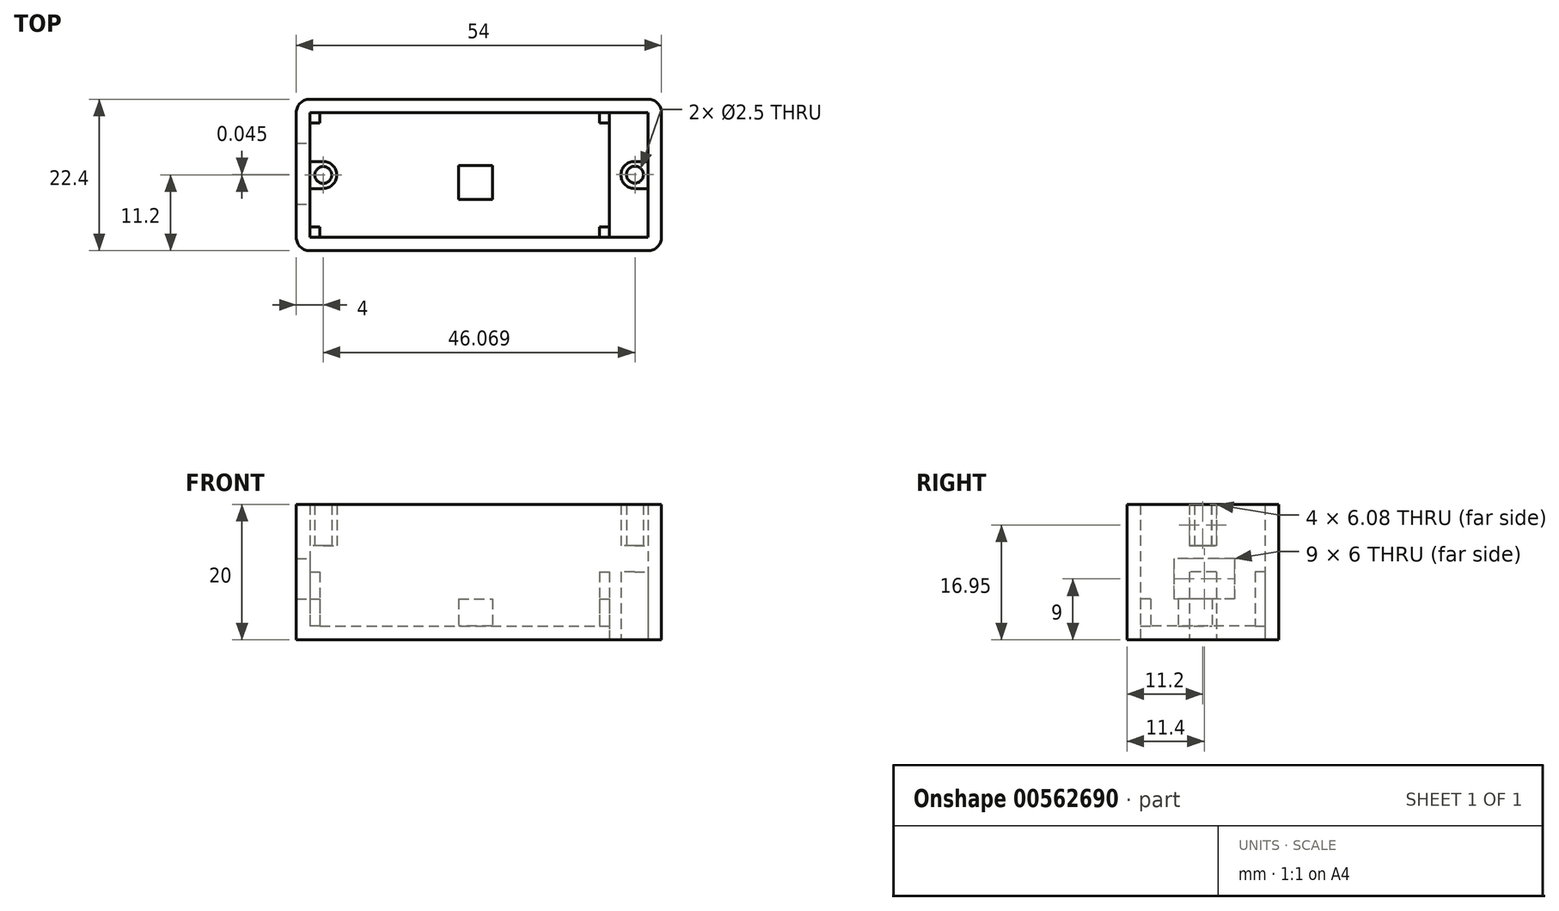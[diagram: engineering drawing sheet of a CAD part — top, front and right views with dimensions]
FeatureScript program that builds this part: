
annotation { "Feature Type Name" : "Feature", "Feature Type Description" : "" }
export const myFeature = defineFeature(function(context is Context, id is Id, definition is map)
    precondition{}
    {
        {
            var Q0;
            Q0=qCreatedBy(makeId("Top.planeOp"),FACE);
            var sketch = newSketch(context, id + "F0", { "sketchPlane" : qUnion([Q0])});
            skLineSegment(sketch, "E0.bottom", {"start": v(-31.58, 11.2) * mm, "end": v(22.42, 11.2) * mm});
            skLineSegment(sketch, "E0.top", {"start": v(-31.58, -11.2) * mm, "end": v(22.42, -11.2) * mm});
            skLineSegment(sketch, "E0.left", {"start": v(-31.58, 11.2) * mm, "end": v(-31.58, -11.2) * mm});
            skLineSegment(sketch, "E0.right", {"start": v(22.42, 11.2) * mm, "end": v(22.42, -11.2) * mm});
            skLineSegment(sketch, "E1.bottom", {"start": v(-29.58, 9.2) * mm, "end": v(20.42, 9.2) * mm});
            skLineSegment(sketch, "E1.top", {"start": v(-29.58, -9.2) * mm, "end": v(20.42, -9.2) * mm});
            skLineSegment(sketch, "E1.left", {"start": v(-29.58, 9.2) * mm, "end": v(-29.58, -9.2) * mm});
            skLineSegment(sketch, "E1.right", {"start": v(20.42, 9.2) * mm, "end": v(20.42, -9.2) * mm});
            skCircle(sketch, "E2", {"center": v(18.42, 0) * mm, "radius": 2 * mm});
            skCircle(sketch, "E3", {"center": v(-27.58, 0) * mm, "radius": 2 * mm});
            skLineSegment(sketch, "E4.bottom", {"start": v(-27.58, -2) * mm, "end": v(-29.58, -2) * mm});
            skLineSegment(sketch, "E4.top", {"start": v(-27.58, 2) * mm, "end": v(-29.58, 2) * mm});
            skLineSegment(sketch, "E4.left", {"start": v(-27.58, -2) * mm, "end": v(-27.58, 2) * mm});
            skLineSegment(sketch, "E4.right", {"start": v(-29.58, -2) * mm, "end": v(-29.58, 2) * mm});
            skLineSegment(sketch, "E5.bottom", {"start": v(18.42, 2) * mm, "end": v(20.42, 2) * mm});
            skLineSegment(sketch, "E5.top", {"start": v(18.42, -2) * mm, "end": v(20.42, -2) * mm});
            skLineSegment(sketch, "E5.left", {"start": v(18.42, 2) * mm, "end": v(18.42, -2) * mm});
            skLineSegment(sketch, "E5.right", {"start": v(20.42, 2) * mm, "end": v(20.42, -2) * mm});
            skCircle(sketch, "E6", {"center": v(-27.58, 0) * mm, "radius": 1.25 * mm});
            skCircle(sketch, "E7", {"center": v(18.49, 0.05) * mm, "radius": 1.25 * mm});
            skLineSegment(sketch, "E8.bottom", {"start": v(-29.58, 9.2) * mm, "end": v(14.72, 9.2) * mm});
            skLineSegment(sketch, "E8.top", {"start": v(-29.58, -9.2) * mm, "end": v(14.72, -9.2) * mm});
            skLineSegment(sketch, "E8.right", {"start": v(14.72, 9.2) * mm, "end": v(14.72, -9.2) * mm});
            skLineSegment(sketch, "E9.bottom", {"start": v(-7.58, 1.37) * mm, "end": v(-2.58, 1.37) * mm});
            skLineSegment(sketch, "E9.top", {"start": v(-7.58, -3.63) * mm, "end": v(-2.58, -3.63) * mm});
            skLineSegment(sketch, "E9.left", {"start": v(-7.58, 1.37) * mm, "end": v(-7.58, -3.63) * mm});
            skLineSegment(sketch, "E9.right", {"start": v(-2.58, 1.37) * mm, "end": v(-2.58, -3.63) * mm});
            skLineSegment(sketch, "E10.bottom", {"start": v(-28.08, 9.2) * mm, "end": v(-29.58, 9.2) * mm});
            skLineSegment(sketch, "E10.top", {"start": v(-28.08, 7.7) * mm, "end": v(-29.58, 7.7) * mm});
            skLineSegment(sketch, "E10.left", {"start": v(-28.08, 9.2) * mm, "end": v(-28.08, 7.7) * mm});
            skLineSegment(sketch, "E10.right", {"start": v(-29.58, 9.2) * mm, "end": v(-29.58, 7.7) * mm});
            skLineSegment(sketch, "E11.bottom", {"start": v(-29.58, -7.7) * mm, "end": v(-28.08, -7.7) * mm});
            skLineSegment(sketch, "E11.top", {"start": v(-29.58, -9.2) * mm, "end": v(-28.08, -9.2) * mm});
            skLineSegment(sketch, "E11.left", {"start": v(-29.58, -7.7) * mm, "end": v(-29.58, -9.2) * mm});
            skLineSegment(sketch, "E11.right", {"start": v(-28.08, -7.7) * mm, "end": v(-28.08, -9.2) * mm});
            skLineSegment(sketch, "E12.bottom", {"start": v(13.22, 9.2) * mm, "end": v(14.72, 9.2) * mm});
            skLineSegment(sketch, "E12.top", {"start": v(13.22, 7.7) * mm, "end": v(14.72, 7.7) * mm});
            skLineSegment(sketch, "E12.left", {"start": v(13.22, 9.2) * mm, "end": v(13.22, 7.7) * mm});
            skLineSegment(sketch, "E12.right", {"start": v(14.72, 9.2) * mm, "end": v(14.72, 7.7) * mm});
            skLineSegment(sketch, "E13.bottom", {"start": v(14.72, -7.7) * mm, "end": v(13.22, -7.7) * mm});
            skLineSegment(sketch, "E13.top", {"start": v(14.72, -9.2) * mm, "end": v(13.22, -9.2) * mm});
            skLineSegment(sketch, "E13.left", {"start": v(14.72, -7.7) * mm, "end": v(14.72, -9.2) * mm});
            skLineSegment(sketch, "E13.right", {"start": v(13.22, -7.7) * mm, "end": v(13.22, -9.2) * mm});
            skSolve(sketch);
        }
        {
            var Q0;
            Q0=qSketchRegion(id+"F0",true);
            extrude(context, id + "F1", {"entities" : qUnion([Q0]), "depth" : 20 * mm});
        }
        {
            var Q0;
            Q0=makeQuery(id+"F0.imprint","IMPRINT",FACE,{"disambiguationData":[TD([[makeQuery(id+"F0.imprint","IMPRINT",EDGE,{"derivedFrom":sQuery(id+"F0.wireOp",EDGE,"E1.bottom")}),-1.0]])]});
            var Q1;
            {var subQ2=sQuery(id+"F0.wireOp",EDGE,"E4.bottom");Q1=makeQuery(id+"F0.imprint","IMPRINT",FACE,{"disambiguationData":[TD([[makeQuery(id+"F0.imprint","IMPRINT",EDGE,{"derivedFrom":subQ2}),1.0]])]});}
            var Q2;
            {var subQ0=sQuery(id+"F0.wireOp",EDGE,"E5.left");var subQ3=sQuery(id+"F0.wireOp",EDGE,"E7");var subQ5=makeQuery(id+"F0.imprint","INTERSECT",VERTEX,{"disambiguationData":[OD(0.0)],"derivedFrom":[subQ0,subQ3]});Q2=makeQuery(id+"F0.imprint","IMPRINT",FACE,{"disambiguationData":[TD([[makeQuery(id+"F0.imprint","IMPRINT",EDGE,{"disambiguationData":[TD([[subQ5,1.0]])],"derivedFrom":subQ3}),-1.0]])]});}
            var Q3;
            {var subQ0=sQuery(id+"F0.wireOp",EDGE,"E5.bottom");Q3=makeQuery(id+"F0.imprint","IMPRINT",FACE,{"disambiguationData":[TD([[makeQuery(id+"F0.imprint","IMPRINT",EDGE,{"derivedFrom":subQ0}),-1.0]])]});}
            var Q4;
            {var subQ0=sQuery(id+"F0.wireOp",EDGE,"E5.top");Q4=makeQuery(id+"F0.imprint","IMPRINT",FACE,{"disambiguationData":[TD([[makeQuery(id+"F0.imprint","IMPRINT",EDGE,{"derivedFrom":subQ0}),1.0]])]});}
            var Q5;
            {var subQ0=sQuery(id+"F0.wireOp",EDGE,"E5.left");var subQ4=sQuery(id+"F0.wireOp",EDGE,"E7");var subQ5=makeQuery(id+"F0.imprint","INTERSECT",VERTEX,{"disambiguationData":[OD(0.0)],"derivedFrom":[subQ0,subQ4]});Q5=makeQuery(id+"F0.imprint","IMPRINT",FACE,{"disambiguationData":[TD([[makeQuery(id+"F0.imprint","IMPRINT",EDGE,{"disambiguationData":[TD([[subQ5,-1.0]])],"derivedFrom":subQ4}),-1.0]])]});}
            var Q6;
            {var subQ0=sQuery(id+"F0.wireOp",EDGE,"E7");var subQ1=sQuery(id+"F0.wireOp",EDGE,"E5.left");var subQ2=makeQuery(id+"F0.imprint","INTERSECT",VERTEX,{"disambiguationData":[OD(0.0)],"derivedFrom":[subQ1,subQ0]});Q6=makeQuery(id+"F0.imprint","IMPRINT",FACE,{"disambiguationData":[TD([[makeQuery(id+"F0.imprint","IMPRINT",EDGE,{"disambiguationData":[TD([[subQ2,-1.0]])],"derivedFrom":subQ1}),-1.0]])]});}
            var Q7;
            {var subQ0=sQuery(id+"F0.wireOp",EDGE,"E7");var subQ1=sQuery(id+"F0.wireOp",EDGE,"E5.left");var subQ2=makeQuery(id+"F0.imprint","INTERSECT",VERTEX,{"disambiguationData":[OD(0.0)],"derivedFrom":[subQ1,subQ0]});Q7=makeQuery(id+"F0.imprint","IMPRINT",FACE,{"disambiguationData":[TD([[makeQuery(id+"F0.imprint","IMPRINT",EDGE,{"disambiguationData":[TD([[subQ2,-1.0]])],"derivedFrom":subQ1}),1.0]])]});}
            var Q8;
            {var subQ0=sQuery(id+"F0.wireOp",EDGE,"E4.top");Q8=makeQuery(id+"F0.imprint","IMPRINT",FACE,{"disambiguationData":[TD([[makeQuery(id+"F0.imprint","IMPRINT",EDGE,{"derivedFrom":subQ0}),1.0]])]});}
            var Q9;
            {var subQ0=sQuery(id+"F0.wireOp",EDGE,"E4.bottom");Q9=makeQuery(id+"F0.imprint","IMPRINT",FACE,{"disambiguationData":[TD([[makeQuery(id+"F0.imprint","IMPRINT",EDGE,{"derivedFrom":subQ0}),-1.0]])]});}
            var Q10;
            {var subQ0=sQuery(id+"F0.wireOp",EDGE,"E4.left");var subQ3=sQuery(id+"F0.wireOp",EDGE,"E6");var subQ6=makeQuery(id+"F0.imprint","INTERSECT",VERTEX,{"disambiguationData":[OD(0.0)],"derivedFrom":[subQ0,subQ3]});Q10=makeQuery(id+"F0.imprint","IMPRINT",FACE,{"disambiguationData":[TD([[makeQuery(id+"F0.imprint","IMPRINT",EDGE,{"disambiguationData":[TD([[subQ6,1.0]])],"derivedFrom":subQ3}),-1.0]])]});}
            var Q11;
            {var subQ0=sQuery(id+"F0.wireOp",EDGE,"E4.left");var subQ4=sQuery(id+"F0.wireOp",EDGE,"E6");var subQ5=makeQuery(id+"F0.imprint","INTERSECT",VERTEX,{"disambiguationData":[OD(0.0)],"derivedFrom":[subQ0,subQ4]});Q11=makeQuery(id+"F0.imprint","IMPRINT",FACE,{"disambiguationData":[TD([[makeQuery(id+"F0.imprint","IMPRINT",EDGE,{"disambiguationData":[TD([[subQ5,-1.0]])],"derivedFrom":subQ4}),-1.0]])]});}
            var Q12;
            {var subQ0=sQuery(id+"F0.wireOp",EDGE,"E6");var subQ1=sQuery(id+"F0.wireOp",EDGE,"E4.left");var subQ2=makeQuery(id+"F0.imprint","INTERSECT",VERTEX,{"disambiguationData":[OD(0.0)],"derivedFrom":[subQ1,subQ0]});Q12=makeQuery(id+"F0.imprint","IMPRINT",FACE,{"disambiguationData":[TD([[makeQuery(id+"F0.imprint","IMPRINT",EDGE,{"disambiguationData":[TD([[subQ2,-1.0]])],"derivedFrom":subQ1}),-1.0]])]});}
            var Q13;
            {var subQ0=sQuery(id+"F0.wireOp",EDGE,"E6");var subQ1=sQuery(id+"F0.wireOp",EDGE,"E4.left");var subQ2=makeQuery(id+"F0.imprint","INTERSECT",VERTEX,{"disambiguationData":[OD(0.0)],"derivedFrom":[subQ1,subQ0]});Q13=makeQuery(id+"F0.imprint","IMPRINT",FACE,{"disambiguationData":[TD([[makeQuery(id+"F0.imprint","IMPRINT",EDGE,{"disambiguationData":[TD([[subQ2,-1.0]])],"derivedFrom":subQ1}),1.0]])]});}
            var Q14;
            Q14=makeQuery(id+"F0.imprint","IMPRINT",FACE,{"disambiguationData":[TD([[makeQuery(id+"F0.imprint","IMPRINT",EDGE,{"derivedFrom":sQuery(id+"F0.wireOp",EDGE,"E9.bottom")}),-1.0]])]});
            var Q15;
            Q15=makeQuery(id+"F0.imprint","IMPRINT",FACE,{"disambiguationData":[TD([[makeQuery(id+"F0.imprint","IMPRINT",EDGE,{"derivedFrom":sQuery(id+"F0.wireOp",EDGE,"E10.bottom")}),1.0]])]});
            var Q16;
            Q16=makeQuery(id+"F0.imprint","IMPRINT",FACE,{"disambiguationData":[TD([[makeQuery(id+"F0.imprint","IMPRINT",EDGE,{"derivedFrom":sQuery(id+"F0.wireOp",EDGE,"E11.bottom")}),-1.0]])]});
            var Q17;
            Q17=makeQuery(id+"F0.imprint","IMPRINT",FACE,{"disambiguationData":[TD([[makeQuery(id+"F0.imprint","IMPRINT",EDGE,{"derivedFrom":sQuery(id+"F0.wireOp",EDGE,"E12.bottom")}),-1.0]])]});
            var Q18;
            Q18=makeQuery(id+"F0.imprint","IMPRINT",FACE,{"disambiguationData":[TD([[makeQuery(id+"F0.imprint","IMPRINT",EDGE,{"derivedFrom":sQuery(id+"F0.wireOp",EDGE,"E13.bottom")}),1.0]])]});
            extrude(context, id + "F2", {"entities" : qUnion([Q0, Q1, Q2, Q3, Q4, Q5, Q6, Q7, Q8, Q9, Q10, Q11, Q12, Q13, Q14, Q15, Q16, Q17, Q18]), "operationType" : NewBodyOperationType.ADD, "depth" : 2 * mm});
        }
        {
            var Q0;
            Q0=qCreatedBy(makeId("Right.planeOp"),FACE);
            var sketch = newSketch(context, id + "F3", { "sketchPlane" : qUnion([Q0])});
            skLineSegment(sketch, "E14.bottom", {"start": v(4.7, 12) * mm, "end": v(-4.3, 12) * mm});
            skLineSegment(sketch, "E14.top", {"start": v(4.7, 6) * mm, "end": v(-4.3, 6) * mm});
            skLineSegment(sketch, "E14.left", {"start": v(4.7, 12) * mm, "end": v(4.7, 6) * mm});
            skLineSegment(sketch, "E14.right", {"start": v(-4.3, 12) * mm, "end": v(-4.3, 6) * mm});
            skSolve(sketch);
        }
        {
            var Q0;
            Q0=makeQuery(id+"F3.imprint","IMPRINT",FACE,{"disambiguationData":[TD([[makeQuery(id+"F3.imprint","IMPRINT",EDGE,{"derivedFrom":sQuery(id+"F3.wireOp",EDGE,"E14.bottom")}),1.0]])]});
            extrude(context, id + "F4", {"entities" : qUnion([Q0]), "operationType" : NewBodyOperationType.REMOVE, "oppositeDirection" : true, "depth" : 35.8 * mm, "hasSecondDirection" : true, "secondDirectionOppositeDirection" : true, "secondDirectionDepth" : 20.2 * mm});
        }
        {
            var Q0;
            {var subQ0=sQuery(id+"F0.wireOp",EDGE,"E5.left");var subQ4=sQuery(id+"F0.wireOp",EDGE,"E7");var subQ5=makeQuery(id+"F0.imprint","INTERSECT",VERTEX,{"disambiguationData":[OD(0.0)],"derivedFrom":[subQ0,subQ4]});Q0=makeQuery(id+"F0.imprint","IMPRINT",FACE,{"disambiguationData":[TD([[makeQuery(id+"F0.imprint","IMPRINT",EDGE,{"disambiguationData":[TD([[subQ5,-1.0]])],"derivedFrom":subQ4}),-1.0]])]});}
            var Q1;
            {var subQ0=sQuery(id+"F0.wireOp",EDGE,"E7");var subQ1=sQuery(id+"F0.wireOp",EDGE,"E5.left");var subQ2=makeQuery(id+"F0.imprint","INTERSECT",VERTEX,{"disambiguationData":[OD(0.0)],"derivedFrom":[subQ1,subQ0]});Q1=makeQuery(id+"F0.imprint","IMPRINT",FACE,{"disambiguationData":[TD([[makeQuery(id+"F0.imprint","IMPRINT",EDGE,{"disambiguationData":[TD([[subQ2,-1.0]])],"derivedFrom":subQ1}),-1.0]])]});}
            var Q2;
            {var subQ0=sQuery(id+"F0.wireOp",EDGE,"E7");var subQ1=sQuery(id+"F0.wireOp",EDGE,"E5.left");var subQ2=makeQuery(id+"F0.imprint","INTERSECT",VERTEX,{"disambiguationData":[OD(0.0)],"derivedFrom":[subQ1,subQ0]});Q2=makeQuery(id+"F0.imprint","IMPRINT",FACE,{"disambiguationData":[TD([[makeQuery(id+"F0.imprint","IMPRINT",EDGE,{"disambiguationData":[TD([[subQ2,-1.0]])],"derivedFrom":subQ1}),1.0]])]});}
            var Q3;
            {var subQ0=sQuery(id+"F0.wireOp",EDGE,"E5.left");var subQ3=sQuery(id+"F0.wireOp",EDGE,"E7");var subQ5=makeQuery(id+"F0.imprint","INTERSECT",VERTEX,{"disambiguationData":[OD(0.0)],"derivedFrom":[subQ0,subQ3]});Q3=makeQuery(id+"F0.imprint","IMPRINT",FACE,{"disambiguationData":[TD([[makeQuery(id+"F0.imprint","IMPRINT",EDGE,{"disambiguationData":[TD([[subQ5,1.0]])],"derivedFrom":subQ3}),-1.0]])]});}
            var Q4;
            {var subQ0=sQuery(id+"F0.wireOp",EDGE,"E5.bottom");Q4=makeQuery(id+"F0.imprint","IMPRINT",FACE,{"disambiguationData":[TD([[makeQuery(id+"F0.imprint","IMPRINT",EDGE,{"derivedFrom":subQ0}),-1.0]])]});}
            var Q5;
            {var subQ0=sQuery(id+"F0.wireOp",EDGE,"E5.top");Q5=makeQuery(id+"F0.imprint","IMPRINT",FACE,{"disambiguationData":[TD([[makeQuery(id+"F0.imprint","IMPRINT",EDGE,{"derivedFrom":subQ0}),1.0]])]});}
            var Q6;
            {var subQ4=sQuery(id+"F0.wireOp",EDGE,"E1.bottom");Q6=makeQuery(id+"F0.imprint","IMPRINT",FACE,{"disambiguationData":[TD([[makeQuery(id+"F0.imprint","IMPRINT",EDGE,{"derivedFrom":subQ4}),-1.0]])]});}
            extrude(context, id + "F5", {"entities" : qUnion([Q0, Q1, Q2, Q3, Q4, Q5, Q6]), "operationType" : NewBodyOperationType.ADD, "depth" : 10 * mm});
        }
        {
            var Q0;
            {var subQ0=sQuery(id+"F0.wireOp",EDGE,"E5.bottom");Q0=makeQuery(id+"F0.imprint","IMPRINT",FACE,{"disambiguationData":[TD([[makeQuery(id+"F0.imprint","IMPRINT",EDGE,{"derivedFrom":subQ0}),-1.0]])]});}
            var Q1;
            {var subQ0=sQuery(id+"F0.wireOp",EDGE,"E5.left");var subQ3=sQuery(id+"F0.wireOp",EDGE,"E7");var subQ5=makeQuery(id+"F0.imprint","INTERSECT",VERTEX,{"disambiguationData":[OD(0.0)],"derivedFrom":[subQ0,subQ3]});Q1=makeQuery(id+"F0.imprint","IMPRINT",FACE,{"disambiguationData":[TD([[makeQuery(id+"F0.imprint","IMPRINT",EDGE,{"disambiguationData":[TD([[subQ5,1.0]])],"derivedFrom":subQ3}),-1.0]])]});}
            var Q2;
            {var subQ0=sQuery(id+"F0.wireOp",EDGE,"E5.top");Q2=makeQuery(id+"F0.imprint","IMPRINT",FACE,{"disambiguationData":[TD([[makeQuery(id+"F0.imprint","IMPRINT",EDGE,{"derivedFrom":subQ0}),1.0]])]});}
            var Q3;
            {var subQ0=sQuery(id+"F0.wireOp",EDGE,"E5.left");var subQ4=sQuery(id+"F0.wireOp",EDGE,"E7");var subQ5=makeQuery(id+"F0.imprint","INTERSECT",VERTEX,{"disambiguationData":[OD(0.0)],"derivedFrom":[subQ0,subQ4]});Q3=makeQuery(id+"F0.imprint","IMPRINT",FACE,{"disambiguationData":[TD([[makeQuery(id+"F0.imprint","IMPRINT",EDGE,{"disambiguationData":[TD([[subQ5,-1.0]])],"derivedFrom":subQ4}),-1.0]])]});}
            var Q4;
            {var subQ0=sQuery(id+"F0.wireOp",EDGE,"E4.top");Q4=makeQuery(id+"F0.imprint","IMPRINT",FACE,{"disambiguationData":[TD([[makeQuery(id+"F0.imprint","IMPRINT",EDGE,{"derivedFrom":subQ0}),1.0]])]});}
            var Q5;
            {var subQ0=sQuery(id+"F0.wireOp",EDGE,"E4.left");var subQ3=sQuery(id+"F0.wireOp",EDGE,"E6");var subQ6=makeQuery(id+"F0.imprint","INTERSECT",VERTEX,{"disambiguationData":[OD(0.0)],"derivedFrom":[subQ0,subQ3]});Q5=makeQuery(id+"F0.imprint","IMPRINT",FACE,{"disambiguationData":[TD([[makeQuery(id+"F0.imprint","IMPRINT",EDGE,{"disambiguationData":[TD([[subQ6,1.0]])],"derivedFrom":subQ3}),-1.0]])]});}
            var Q6;
            {var subQ0=sQuery(id+"F0.wireOp",EDGE,"E4.left");var subQ4=sQuery(id+"F0.wireOp",EDGE,"E6");var subQ5=makeQuery(id+"F0.imprint","INTERSECT",VERTEX,{"disambiguationData":[OD(0.0)],"derivedFrom":[subQ0,subQ4]});Q6=makeQuery(id+"F0.imprint","IMPRINT",FACE,{"disambiguationData":[TD([[makeQuery(id+"F0.imprint","IMPRINT",EDGE,{"disambiguationData":[TD([[subQ5,-1.0]])],"derivedFrom":subQ4}),-1.0]])]});}
            var Q7;
            {var subQ0=sQuery(id+"F0.wireOp",EDGE,"E4.bottom");Q7=makeQuery(id+"F0.imprint","IMPRINT",FACE,{"disambiguationData":[TD([[makeQuery(id+"F0.imprint","IMPRINT",EDGE,{"derivedFrom":subQ0}),-1.0]])]});}
            extrude(context, id + "F6", {"entities" : qUnion([Q0, Q1, Q2, Q3, Q4, Q5, Q6, Q7]), "operationType" : NewBodyOperationType.ADD, "depth" : 20 * mm, "hasSecondDirection" : true, "secondDirectionOppositeDirection" : false, "secondDirectionDepth" : 13.9 * mm});
        }
        {
            var Q0;
            Q0=makeQuery(id+"F1.opExtrude","SWEPT_EDGE",EDGE,{"disambiguationData":[OSD([sQuery(id+"F0.wireOp",EDGE,"E0.top"),sQuery(id+"F0.wireOp",EDGE,"E0.left")])]});
            var Q1;
            Q1=makeQuery(id+"F1.opExtrude","SWEPT_EDGE",EDGE,{"disambiguationData":[OSD([sQuery(id+"F0.wireOp",EDGE,"E0.bottom"),sQuery(id+"F0.wireOp",EDGE,"E0.left")])]});
            var Q2;
            Q2=makeQuery(id+"F1.opExtrude","SWEPT_EDGE",EDGE,{"disambiguationData":[OSD([sQuery(id+"F0.wireOp",EDGE,"E0.bottom"),sQuery(id+"F0.wireOp",EDGE,"E0.right")])]});
            var Q3;
            Q3=makeQuery(id+"F6.opExtrude","SWEPT_EDGE",EDGE,{"disambiguationData":[OSD([sQuery(id+"F0.wireOp",EDGE,"E4.top"),sQuery(id+"F0.wireOp",EDGE,"E1.left")])]});
            var Q4;
            Q4=makeQuery(id+"F6.opExtrude","SWEPT_EDGE",EDGE,{"disambiguationData":[OSD([sQuery(id+"F0.wireOp",EDGE,"E4.bottom"),sQuery(id+"F0.wireOp",EDGE,"E1.left")])]});
            var Q5;
            Q5=makeQuery(id+"F6.opExtrude","SWEPT_EDGE",EDGE,{"disambiguationData":[OSD([sQuery(id+"F0.wireOp",EDGE,"E1.right"),sQuery(id+"F0.wireOp",EDGE,"E5.top"),sQuery(id+"F0.wireOp",EDGE,"E5.right")])]});
            var Q6;
            Q6=makeQuery(id+"F6.opExtrude","SWEPT_EDGE",EDGE,{"disambiguationData":[OSD([sQuery(id+"F0.wireOp",EDGE,"E1.right"),sQuery(id+"F0.wireOp",EDGE,"E5.bottom"),sQuery(id+"F0.wireOp",EDGE,"E5.right")])]});
            var Q7;
            Q7=makeQuery(id+"F1.opExtrude","SWEPT_EDGE",EDGE,{"disambiguationData":[OSD([sQuery(id+"F0.wireOp",EDGE,"E0.top"),sQuery(id+"F0.wireOp",EDGE,"E0.right")])]});
            fillet(context, id + "F7", {"entities" : qUnion([Q0, Q1, Q2, Q3, Q4, Q5, Q6, Q7]), "radius" : 2 * mm, "tangentPropagation" : true, "allowEdgeOverflow" : false});
        }
        {
            var Q0;
            Q0=makeQuery(id+"F0.imprint","IMPRINT",FACE,{"disambiguationData":[TD([[makeQuery(id+"F0.imprint","IMPRINT",EDGE,{"derivedFrom":sQuery(id+"F0.wireOp",EDGE,"E9.bottom")}),-1.0]])]});
            var Q1;
            Q1=makeQuery(id+"F0.imprint","IMPRINT",FACE,{"disambiguationData":[TD([[makeQuery(id+"F0.imprint","IMPRINT",EDGE,{"derivedFrom":sQuery(id+"F0.wireOp",EDGE,"E10.bottom")}),1.0]])]});
            var Q2;
            Q2=makeQuery(id+"F0.imprint","IMPRINT",FACE,{"disambiguationData":[TD([[makeQuery(id+"F0.imprint","IMPRINT",EDGE,{"derivedFrom":sQuery(id+"F0.wireOp",EDGE,"E11.bottom")}),-1.0]])]});
            var Q3;
            Q3=makeQuery(id+"F0.imprint","IMPRINT",FACE,{"disambiguationData":[TD([[makeQuery(id+"F0.imprint","IMPRINT",EDGE,{"derivedFrom":sQuery(id+"F0.wireOp",EDGE,"E12.bottom")}),-1.0]])]});
            var Q4;
            Q4=makeQuery(id+"F0.imprint","IMPRINT",FACE,{"disambiguationData":[TD([[makeQuery(id+"F0.imprint","IMPRINT",EDGE,{"derivedFrom":sQuery(id+"F0.wireOp",EDGE,"E13.bottom")}),1.0]])]});
            extrude(context, id + "F8", {"entities" : qUnion([Q0, Q1, Q2, Q3, Q4]), "operationType" : NewBodyOperationType.ADD, "depth" : 6 * mm});
        }
    });
